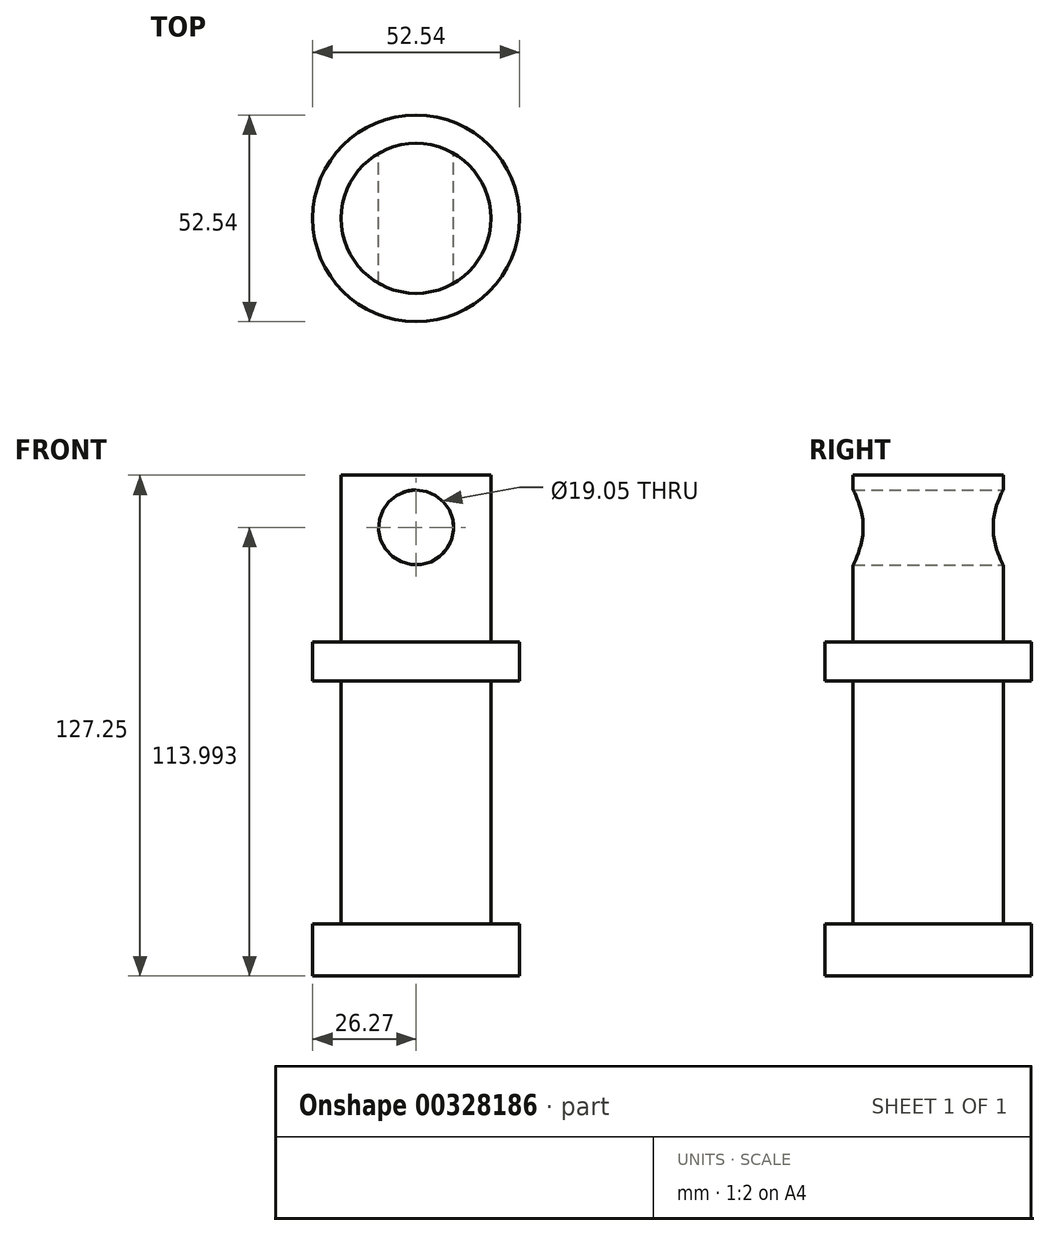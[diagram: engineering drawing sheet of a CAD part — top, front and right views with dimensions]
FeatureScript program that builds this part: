
annotation { "Feature Type Name" : "Feature", "Feature Type Description" : "" }
export const myFeature = defineFeature(function(context is Context, id is Id, definition is map)
    precondition{}
    {
        {
            var Q0;
            Q0=qCreatedBy(makeId("Top.planeOp"),FACE);
            var sketch = newSketch(context, id + "F0", { "sketchPlane" : qUnion([Q0])});
            skCircle(sketch, "E0", {"center": v(0, 0) * mm, "radius": 19.05 * mm});
            skSolve(sketch);
        }
        {
            var Q0;
            Q0 = qSketchRegion(id + "F0", true);
            extrude(context, id + "F1", {"entities" : qUnion([Q0]), "endBound" : BoundingType.SYMMETRIC, "depth" : 127 * mm});
        }
        {
            var Q0;
            Q0=qCreatedBy(makeId("Front.planeOp"),FACE);
            var sketch = newSketch(context, id + "F2", { "sketchPlane" : qUnion([Q0])});
            skPoint(sketch, "E1", {"position": v(0, 50.24) * mm});
            skSolve(sketch);
        }
        {
            var Q0;
            Q0=sQuery(id+"F2.wireOp",VERTEX,"E1");
            var Q1;
            Q1=makeQuery(id+"F1.opExtrude","SWEPT_BODY",BODY,{"disambiguationData":[OSD([sQuery(id+"F0.wireOp",EDGE,"E0")])]});
            hole(context, id + "F3", {"style" : HoleStyle.SIMPLE, "endStyle" : HoleEndStyle.THROUGH, "oppositeDirection" : true, "holeDiameter" : 19.05 * mm, "tappedDepth" : 12.7 * mm, "tapClearance" : 3, "locations" : qUnion([Q0]), "scope" : qUnion([Q1])});
        }
        {
            var Q0;
            Q0=sQuery(id+"F2.wireOp",VERTEX,"E1");
            var Q1;
            Q1=makeQuery(id+"F1.opExtrude","SWEPT_BODY",BODY,{"disambiguationData":[OSD([sQuery(id+"F0.wireOp",EDGE,"E0")])]});
            hole(context, id + "F4", {"style" : HoleStyle.SIMPLE, "endStyle" : HoleEndStyle.THROUGH, "holeDiameter" : 19.05 * mm, "tappedDepth" : 12.7 * mm, "tapClearance" : 3, "locations" : qUnion([Q0]), "scope" : qUnion([Q1])});
        }
        {
            var Q0;
            Q0=qCreatedBy(makeId("Top.planeOp"),FACE);
            var sketch = newSketch(context, id + "F5", { "sketchPlane" : qUnion([Q0])});
            skCircle(sketch, "E2", {"center": v(0, 0) * mm, "radius": 26.27 * mm});
            skSolve(sketch);
        }
        {
            var Q0;
            Q0=makeQuery(id+"F5.imprint","IMPRINT",FACE,{"disambiguationData":[TD([[makeQuery(id+"F5.imprint","IMPRINT",EDGE,{"derivedFrom":sQuery(id+"F5.wireOp",EDGE,"E2")}),1.0]])]});
            extrude(context, id + "F6", {"entities" : qUnion([Q0]), "operationType" : NewBodyOperationType.ADD, "oppositeDirection" : true, "depth" : 63.75 * mm, "hasSecondDirection" : true, "secondDirectionOppositeDirection" : true, "secondDirectionDepth" : 50.55 * mm});
        }
        {
            var Q0;
            Q0 = qSketchRegion(id + "F5", true);
            extrude(context, id + "F7", {"entities" : qUnion([Q0]), "operationType" : NewBodyOperationType.ADD, "depth" : 21.08 * mm, "hasSecondDirection" : true, "secondDirectionOppositeDirection" : false, "secondDirectionDepth" : 11.18 * mm});
        }
    });
